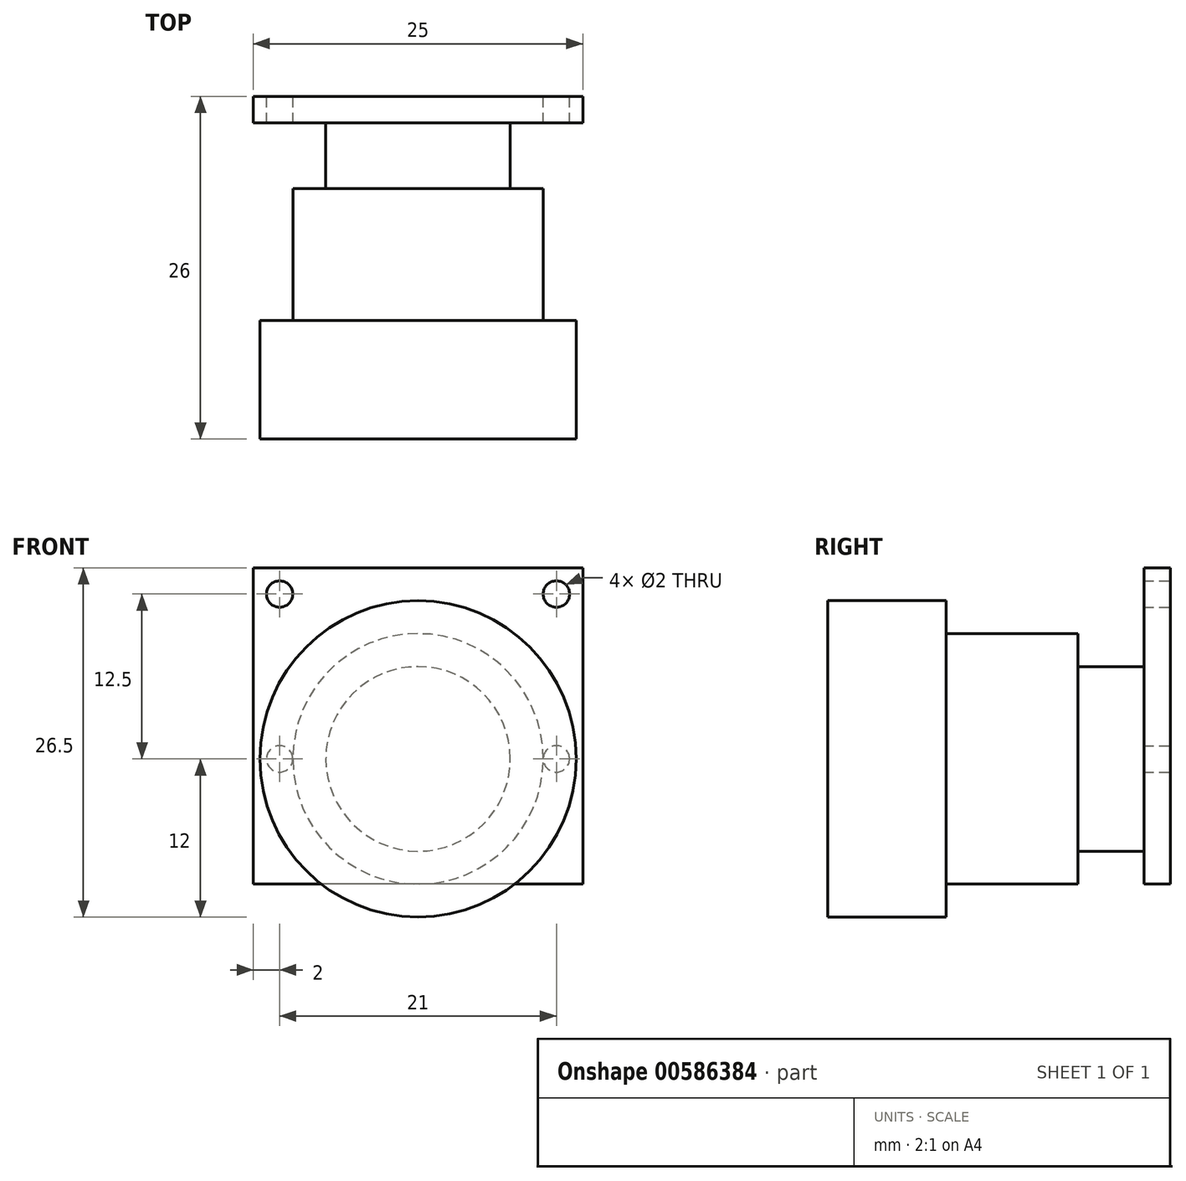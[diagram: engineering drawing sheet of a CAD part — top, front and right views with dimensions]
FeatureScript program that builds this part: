
annotation { "Feature Type Name" : "Feature", "Feature Type Description" : "" }
export const myFeature = defineFeature(function(context is Context, id is Id, definition is map)
    precondition{}
    {
        {
            var Q0;
            Q0=qCreatedBy(makeId("Front.planeOp"),FACE);
            var sketch = newSketch(context, id + "F0", { "sketchPlane" : qUnion([Q0])});
            skLineSegment(sketch, "E0.bottom", {"start": v(12.5, -9.5) * mm, "end": v(-12.5, -9.5) * mm});
            skLineSegment(sketch, "E0.top", {"start": v(12.5, 14.5) * mm, "end": v(-12.5, 14.5) * mm});
            skLineSegment(sketch, "E0.left", {"start": v(12.5, -9.5) * mm, "end": v(12.5, 14.5) * mm});
            skLineSegment(sketch, "E0.right", {"start": v(-12.5, -9.5) * mm, "end": v(-12.5, 14.5) * mm});
            skPoint(sketch, "E0.middle", {"position": v(0, 0) * mm});
            skCircle(sketch, "E1", {"center": v(0, 0) * mm, "radius": 7 * mm});
            skCircle(sketch, "E2", {"center": v(-10.5, 12.5) * mm, "radius": 1 * mm});
            skCircle(sketch, "E3.MirrorC", {"center": v(10.5, 12.5) * mm, "radius": 1 * mm});
            skCircle(sketch, "E4.MirrorC", {"center": v(10.5, 0) * mm, "radius": 1 * mm});
            skCircle(sketch, "E5.MirrorC", {"center": v(-10.5, 0) * mm, "radius": 1 * mm});
            skSolve(sketch);
        }
        {
            var Q0;
            Q0=makeQuery(id+"F0.imprint","IMPRINT",FACE,{"disambiguationData":[TD([[makeQuery(id+"F0.imprint","IMPRINT",EDGE,{"derivedFrom":sQuery(id+"F0.wireOp",EDGE,"E0.bottom")}),-1.0]])]});
            var Q1;
            Q1=makeQuery(id+"F0.imprint","IMPRINT",FACE,{"disambiguationData":[TD([[makeQuery(id+"F0.imprint","IMPRINT",EDGE,{"derivedFrom":sQuery(id+"F0.wireOp",EDGE,"E1")}),1.0]])]});
            extrude(context, id + "F1", {"entities" : qUnion([Q0, Q1]), "depth" : 2 * mm});
        }
        {
            var Q0;
            Q0=makeQuery(id+"F0.imprint","IMPRINT",FACE,{"disambiguationData":[TD([[makeQuery(id+"F0.imprint","IMPRINT",EDGE,{"derivedFrom":sQuery(id+"F0.wireOp",EDGE,"E1")}),1.0]])]});
            var Q1;
            Q1=sQuery(id+"F0.wireOp",EDGE,"E1");
            extrude(context, id + "F2", {"entities" : qUnion([Q0]), "operationType" : NewBodyOperationType.ADD, "surfaceEntities" : qUnion([Q1]), "depth" : 24 * mm});
        }
        {
            var Q0;
            Q0=qCreatedBy(makeId("Front.planeOp"),FACE);
            var sketch = newSketch(context, id + "F3", { "sketchPlane" : qUnion([Q0])});
            skCircle(sketch, "E6", {"center": v(0, 0) * mm, "radius": 12 * mm});
            skCircle(sketch, "E7", {"center": v(0, 0) * mm, "radius": 6 * mm});
            skCircle(sketch, "E8", {"center": v(0, 0) * mm, "radius": 9.5 * mm});
            skSolve(sketch);
        }
        {
            var Q0;
            Q0=makeQuery(id+"F3.imprint","IMPRINT",FACE,{"disambiguationData":[TD([[makeQuery(id+"F3.imprint","IMPRINT",EDGE,{"derivedFrom":sQuery(id+"F3.wireOp",EDGE,"E7")}),1.0]])]});
            extrude(context, id + "F4", {"entities" : qUnion([Q0]), "depth" : 7 * mm});
        }
        {
            var Q0;
            Q0=makeQuery(id+"F3.imprint","IMPRINT",FACE,{"disambiguationData":[TD([[makeQuery(id+"F3.imprint","IMPRINT",EDGE,{"derivedFrom":sQuery(id+"F3.wireOp",EDGE,"E7")}),-1.0]])]});
            var Q1;
            Q1=makeQuery(id+"F3.imprint","IMPRINT",FACE,{"disambiguationData":[TD([[makeQuery(id+"F3.imprint","IMPRINT",EDGE,{"derivedFrom":sQuery(id+"F3.wireOp",EDGE,"E7")}),1.0]])]});
            extrude(context, id + "F5", {"entities" : qUnion([Q0, Q1]), "operationType" : NewBodyOperationType.ADD, "depth" : 17 * mm, "hasSecondDirection" : true, "secondDirectionOppositeDirection" : false, "secondDirectionDepth" : 7 * mm});
        }
        {
            var Q0;
            Q0=makeQuery(id+"F3.imprint","IMPRINT",FACE,{"disambiguationData":[TD([[makeQuery(id+"F3.imprint","IMPRINT",EDGE,{"derivedFrom":sQuery(id+"F3.wireOp",EDGE,"E6")}),1.0]])]});
            var Q1;
            Q1=makeQuery(id+"F3.imprint","IMPRINT",FACE,{"disambiguationData":[TD([[makeQuery(id+"F3.imprint","IMPRINT",EDGE,{"derivedFrom":sQuery(id+"F3.wireOp",EDGE,"E7")}),-1.0]])]});
            var Q2;
            Q2=makeQuery(id+"F3.imprint","IMPRINT",FACE,{"disambiguationData":[TD([[makeQuery(id+"F3.imprint","IMPRINT",EDGE,{"derivedFrom":sQuery(id+"F3.wireOp",EDGE,"E7")}),1.0]])]});
            extrude(context, id + "F6", {"entities" : qUnion([Q0, Q1, Q2]), "operationType" : NewBodyOperationType.ADD, "depth" : 26 * mm, "hasSecondDirection" : true, "secondDirectionOppositeDirection" : false, "secondDirectionDepth" : 17 * mm});
        }
    });
